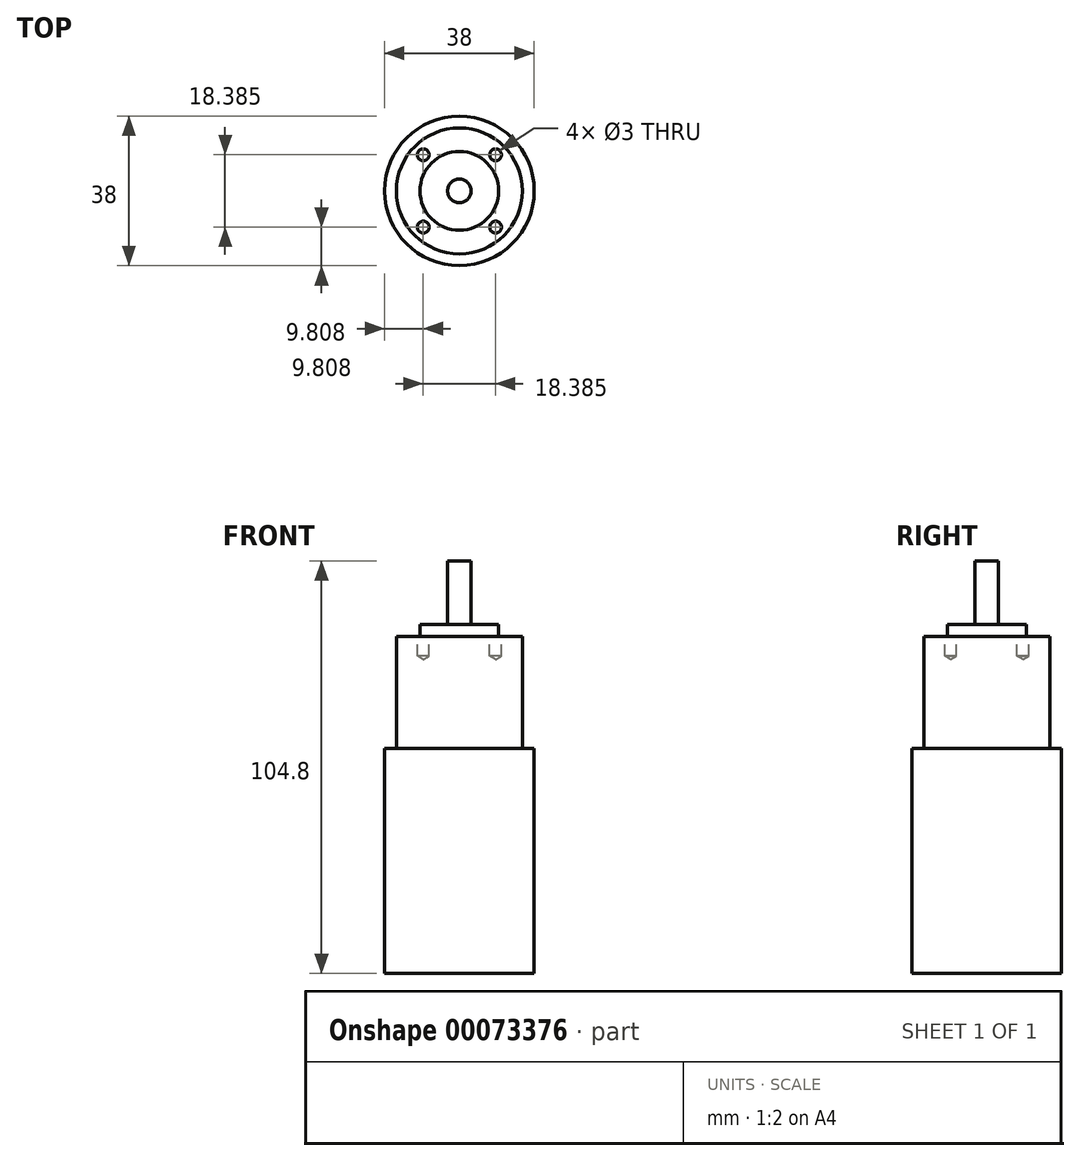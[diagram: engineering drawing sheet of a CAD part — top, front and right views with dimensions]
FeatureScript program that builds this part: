
annotation { "Feature Type Name" : "Feature", "Feature Type Description" : "" }
export const myFeature = defineFeature(function(context is Context, id is Id, definition is map)
    precondition{}
    {
        {
            var Q0;
            Q0=qCreatedBy(makeId("Top.planeOp"),FACE);
            var sketch = newSketch(context, id + "F0", { "sketchPlane" : qUnion([Q0])});
            skCircle(sketch, "E0", {"center": v(0, 0) * mm, "radius": 19 * mm});
            skSolve(sketch);
        }
        {
            var Q0;
            Q0=makeQuery(id+"F0.imprint","IMPRINT",FACE,{"disambiguationData":[TD([[makeQuery(id+"F0.imprint","IMPRINT",EDGE,{"derivedFrom":sQuery(id+"F0.wireOp",EDGE,"E0")}),1.0]])]});
            extrude(context, id + "F1", {"entities" : qUnion([Q0]), "depth" : 57.1 * mm, "offsetDistance" : 25 * mm});
        }
        {
            var Q0;
            Q0=makeQuery(id+"F1.opExtrude","CAP_FACE",FACE,{"disambiguationData":[OSD([sQuery(id+"F0.wireOp",EDGE,"E0")])],"isStart":false});
            var sketch = newSketch(context, id + "F2", { "sketchPlane" : qUnion([Q0])});
            skCircle(sketch, "E1", {"center": v(0, 0) * mm, "radius": 16 * mm});
            skSolve(sketch);
        }
        {
            var Q0;
            Q0=makeQuery(id+"F2.imprint","IMPRINT",FACE,{"disambiguationData":[TD([[makeQuery(id+"F2.imprint","IMPRINT",EDGE,{"derivedFrom":sQuery(id+"F2.wireOp",EDGE,"E1")}),1.0]])]});
            extrude(context, id + "F3", {"entities" : qUnion([Q0]), "operationType" : NewBodyOperationType.ADD, "depth" : 28.5 * mm, "offsetDistance" : 25 * mm});
        }
        {
            var Q0;
            Q0=makeQuery(id+"F3.opExtrude","CAP_FACE",FACE,{"disambiguationData":[OSD([sQuery(id+"F2.wireOp",EDGE,"E1")])],"isStart":false});
            var sketch = newSketch(context, id + "F4", { "sketchPlane" : qUnion([Q0])});
            skCircle(sketch, "E2", {"center": v(0, 0) * mm, "radius": 10 * mm});
            skSolve(sketch);
        }
        {
            var Q0;
            Q0=qSketchRegion(id+"F4",true);
            extrude(context, id + "F5", {"entities" : qUnion([Q0]), "operationType" : NewBodyOperationType.ADD, "depth" : 3 * mm, "offsetDistance" : 25 * mm});
        }
        {
            var Q0;
            Q0=makeQuery(id+"F5.opExtrude","CAP_FACE",FACE,{"disambiguationData":[OSD([sQuery(id+"F4.wireOp",EDGE,"E2")])],"isStart":false});
            var sketch = newSketch(context, id + "F6", { "sketchPlane" : qUnion([Q0])});
            skCircle(sketch, "E3", {"center": v(0, 0) * mm, "radius": 3 * mm});
            skSolve(sketch);
        }
        {
            var Q0;
            Q0=qSketchRegion(id+"F6",true);
            extrude(context, id + "F7", {"entities" : qUnion([Q0]), "operationType" : NewBodyOperationType.ADD, "depth" : (19.2 - 3) * mm, "offsetDistance" : 25 * mm});
        }
        {
            var Q0;
            Q0=makeQuery(id+"F3.opExtrude","CAP_FACE",FACE,{"disambiguationData":[OSD([sQuery(id+"F2.wireOp",EDGE,"E1")])],"isStart":false});
            var sketch = newSketch(context, id + "F8", { "sketchPlane" : qUnion([Q0])});
            skCircle(sketch, "E4", {"center": v(0, 0) * mm, "radius": 13 * mm});
            skLineSegment(sketch, "E5.bottom", {"start": v(-9.2, 9.2) * mm, "end": v(9.2, 9.2) * mm});
            skLineSegment(sketch, "E5.top", {"start": v(-9.2, -9.2) * mm, "end": v(9.2, -9.2) * mm});
            skLineSegment(sketch, "E5.left", {"start": v(-9.2, 9.2) * mm, "end": v(-9.2, -9.2) * mm});
            skLineSegment(sketch, "E5.right", {"start": v(9.2, 9.2) * mm, "end": v(9.2, -9.2) * mm});
            skSolve(sketch);
        }
        {
            var Q0;
            Q0=sQuery(id+"F8.wireOp",VERTEX,"E5.bottom.start");
            var Q1;
            Q1=sQuery(id+"F8.wireOp",VERTEX,"E5.bottom.end");
            var Q2;
            Q2=sQuery(id+"F8.wireOp",VERTEX,"E5.top.end");
            var Q3;
            Q3=sQuery(id+"F8.wireOp",VERTEX,"E5.top.start");
            var Q4;
            Q4=makeQuery(id+"F1.opExtrude","SWEPT_BODY",BODY,{"disambiguationData":[OSD([sQuery(id+"F0.wireOp",EDGE,"E0")])]});
            hole(context, id + "F9", {"style" : HoleStyle.SIMPLE, "endStyle" : HoleEndStyle.BLIND, "holeDiameter" : 3 * mm, "majorDiameter" : 5 * mm, "holeDepth" : 5 * mm, "tappedDepth" : 12 * mm, "tapClearance" : 3, "locations" : qUnion([Q0, Q1, Q2, Q3]), "scope" : qUnion([Q4])});
        }
    });
